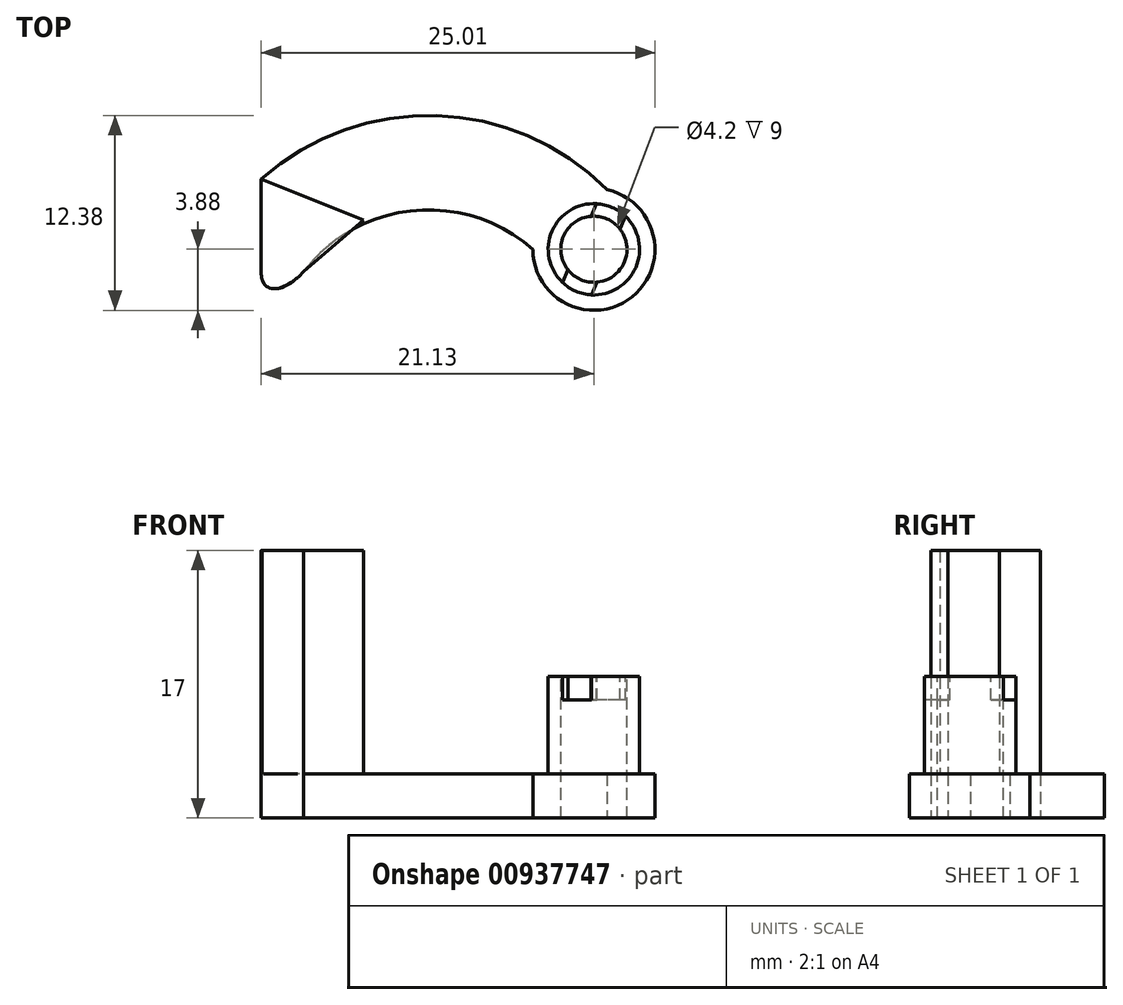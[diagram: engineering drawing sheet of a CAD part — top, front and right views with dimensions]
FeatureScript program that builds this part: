
annotation { "Feature Type Name" : "Feature", "Feature Type Description" : "" }
export const myFeature = defineFeature(function(context is Context, id is Id, definition is map)
    precondition{}
    {
        {
            var Q0;
            Q0=qCreatedBy(makeId("Top.planeOp"),FACE);
            var sketch = newSketch(context, id + "F0", { "sketchPlane" : qUnion([Q0])});
            skCircle(sketch, "E0", {"center": v(-23, -5) * mm, "radius": 10 * mm});
            skCircle(sketch, "E1", {"center": v(-23, -5) * mm, "radius": 16 * mm});
            skCircle(sketch, "E2", {"center": v(-12.5, 2.5) * mm, "radius": 3.88 * mm});
            skLineSegment(sketch, "E3", {"start": v(-33.62, 6.96) * mm, "end": v(-33.62, 0.96) * mm});
            skFitSpline(sketch, "E4", {"points": [v(-33.62, 0.96) * mm, v(-32.74, 0) * mm, v(-30.43, 1.69) * mm], "startDerivative": vector(0.03, -5.56) * mm, "endDerivative": vector(4.63, 6) * mm});
            skSolve(sketch);
        }
        {
            var Q0;
            {var subQ0=sQuery(id+"F0.wireOp",EDGE,"E3");Q0=makeQuery(id+"F0.imprint","IMPRINT",FACE,{"disambiguationData":[TD([[makeQuery(id+"F0.imprint","IMPRINT",EDGE,{"derivedFrom":subQ0}),1.0]])]});}
            var Q1;
            {var subQ0=sQuery(id+"F0.wireOp",EDGE,"E2");var subQ1=sQuery(id+"F0.wireOp",EDGE,"E0");var subQ2=makeQuery(id+"F0.imprint","INTERSECT",VERTEX,{"disambiguationData":[OD(0.0)],"derivedFrom":[subQ1,subQ0]});Q1=makeQuery(id+"F0.imprint","IMPRINT",FACE,{"disambiguationData":[TD([[makeQuery(id+"F0.imprint","IMPRINT",EDGE,{"disambiguationData":[TD([[subQ2,1.0]])],"derivedFrom":subQ1}),-1.0]])]});}
            var Q2;
            {var subQ0=sQuery(id+"F0.wireOp",EDGE,"E2");var subQ1=sQuery(id+"F0.wireOp",EDGE,"E0");var subQ2=makeQuery(id+"F0.imprint","INTERSECT",VERTEX,{"disambiguationData":[OD(0.0)],"derivedFrom":[subQ1,subQ0]});Q2=makeQuery(id+"F0.imprint","IMPRINT",FACE,{"disambiguationData":[TD([[makeQuery(id+"F0.imprint","IMPRINT",EDGE,{"disambiguationData":[TD([[subQ2,1.0]])],"derivedFrom":subQ1}),1.0]])]});}
            var Q3;
            {var subQ0=sQuery(id+"F0.wireOp",EDGE,"E2");var subQ1=sQuery(id+"F0.wireOp",EDGE,"E1");var subQ2=makeQuery(id+"F0.imprint","INTERSECT",VERTEX,{"disambiguationData":[OD(0.0)],"derivedFrom":[subQ1,subQ0]});Q3=makeQuery(id+"F0.imprint","IMPRINT",FACE,{"disambiguationData":[TD([[makeQuery(id+"F0.imprint","IMPRINT",EDGE,{"disambiguationData":[TD([[subQ2,1.0]])],"derivedFrom":subQ1}),-1.0]])]});}
            extrude(context, id + "F1", {"entities" : qUnion([Q0, Q1, Q2, Q3]), "depth" : 2.8 * mm, "offsetDistance" : 25 * mm});
        }
        {
            var Q0;
            Q0=makeQuery(id+"F1.opExtrude","CAP_FACE",FACE,{"disambiguationData":[OSD([sQuery(id+"F0.wireOp",EDGE,"E0"),sQuery(id+"F0.wireOp",EDGE,"E1"),sQuery(id+"F0.wireOp",EDGE,"E2"),sQuery(id+"F0.wireOp",EDGE,"E3"),sQuery(id+"F0.wireOp",EDGE,"E4")])],"isStart":false});
            var sketch = newSketch(context, id + "F2", { "sketchPlane" : qUnion([Q0])});
            skCircle(sketch, "E5", {"center": v(-12.5, 2.5) * mm, "radius": 2.9 * mm});
            skSolve(sketch);
        }
        {
            var Q0;
            Q0 = qSketchRegion(id + "F2", true);
            extrude(context, id + "F3", {"entities" : qUnion([Q0]), "operationType" : NewBodyOperationType.ADD, "depth" : 6.2 * mm, "offsetDistance" : 25 * mm});
        }
        {
            var Q0;
            Q0=makeQuery(id+"F1.opExtrude","CAP_FACE",FACE,{"disambiguationData":[OSD([sQuery(id+"F0.wireOp",EDGE,"E0"),sQuery(id+"F0.wireOp",EDGE,"E1"),sQuery(id+"F0.wireOp",EDGE,"E2"),sQuery(id+"F0.wireOp",EDGE,"E3"),sQuery(id+"F0.wireOp",EDGE,"E4")])],"isStart":false});
            var sketch = newSketch(context, id + "F4", { "sketchPlane" : qUnion([Q0])});
            skLineSegment(sketch, "E6", {"start": v(-33.62, 6.96) * mm, "end": v(-33.62, 0.96) * mm});
            skFitSpline(sketch, "E7", {"points": [v(-33.62, 0.96) * mm, v(-32.74, 0) * mm, v(-30.93, 1.1) * mm], "startDerivative": vector(0, -4.72) * mm, "endDerivative": vector(2.22, 2.7) * mm});
            skLineSegment(sketch, "E8", {"start": v(-30.93, 1.1) * mm, "end": v(-27.13, 4.34) * mm});
            skLineSegment(sketch, "E9", {"start": v(-27.13, 4.34) * mm, "end": v(-33.62, 6.96) * mm});
            skSolve(sketch);
        }
        {
            var Q0;
            Q0 = qSketchRegion(id + "F4", true);
            extrude(context, id + "F5", {"entities" : qUnion([Q0]), "operationType" : NewBodyOperationType.ADD, "depth" : 14.2 * mm, "offsetDistance" : 25 * mm});
        }
        {
            var Q0;
            Q0=makeQuery(id+"F3.opExtrude","CAP_FACE",FACE,{"disambiguationData":[OSD([sQuery(id+"F2.wireOp",EDGE,"E5")])],"isStart":false});
            var sketch = newSketch(context, id + "F6", { "sketchPlane" : qUnion([Q0])});
            skCircle(sketch, "E10", {"center": v(-12.5, 2.5) * mm, "radius": 2.9 * mm});
            skLineSegment(sketch, "E11", {"start": v(-12.34, 5.4) * mm, "end": v(-10.5, 4.6) * mm});
            skLineSegment(sketch, "E12", {"start": v(-10.5, 4.6) * mm, "end": v(-12.66, -0.4) * mm});
            skLineSegment(sketch, "E13", {"start": v(-12.66, -0.4) * mm, "end": v(-14.5, 0.4) * mm});
            skLineSegment(sketch, "E14", {"start": v(-14.5, 0.4) * mm, "end": v(-12.34, 5.4) * mm});
            skSolve(sketch);
        }
        {
            var Q0;
            Q0=makeQuery(id+"F6.imprint","IMPRINT",FACE,{"disambiguationData":[TD([[makeQuery(id+"F6.imprint","IMPRINT",EDGE,{"derivedFrom":sQuery(id+"F6.wireOp",EDGE,"E11")}),-1.0]])]});
            var Q1;
            {var subQ0=sQuery(id+"F6.wireOp",EDGE,"E13");Q1=makeQuery(id+"F6.imprint","IMPRINT",FACE,{"disambiguationData":[TD([[makeQuery(id+"F6.imprint","IMPRINT",EDGE,{"derivedFrom":subQ0}),1.0]])]});}
            var Q2;
            {var subQ0=sQuery(id+"F6.wireOp",EDGE,"E11");Q2=makeQuery(id+"F6.imprint","IMPRINT",FACE,{"disambiguationData":[TD([[makeQuery(id+"F6.imprint","IMPRINT",EDGE,{"derivedFrom":subQ0}),1.0]])]});}
            extrude(context, id + "F7", {"entities" : qUnion([Q0, Q1, Q2]), "operationType" : NewBodyOperationType.REMOVE, "oppositeDirection" : true, "depth" : 1.5 * mm, "offsetDistance" : 25 * mm});
        }
        {
            var Q0;
            Q0=makeQuery(id+"F7.boolean.opBoolean","COPY",FACE,{"derivedFrom":makeQuery(id+"F7.opExtrude","CAP_FACE",FACE,{"disambiguationData":[OSD([sQuery(id+"F6.wireOp",EDGE,"E10"),sQuery(id+"F6.wireOp",EDGE,"CRHT1Mvr-lyfj-ZwRk-eIFm-zqhd7q6KrsdK.left"),sQuery(id+"F6.wireOp",EDGE,"CRHT1Mvr-lyfj-ZwRk-eIFm-zqhd7q6KrsdK.right")])],"isStart":false})});
            var sketch = newSketch(context, id + "F8", { "sketchPlane" : qUnion([Q0])});
            skCircle(sketch, "E15", {"center": v(-12.5, 2.5) * mm, "radius": 2.1 * mm});
            skSolve(sketch);
        }
        {
            var Q0;
            Q0 = qSketchRegion(id + "F8", true);
            extrude(context, id + "F9", {"entities" : qUnion([Q0]), "operationType" : NewBodyOperationType.REMOVE, "endBound" : BoundingType.SYMMETRIC, "oppositeDirection" : true, "depth" : 25 * mm, "offsetDistance" : 25 * mm});
        }
    });
